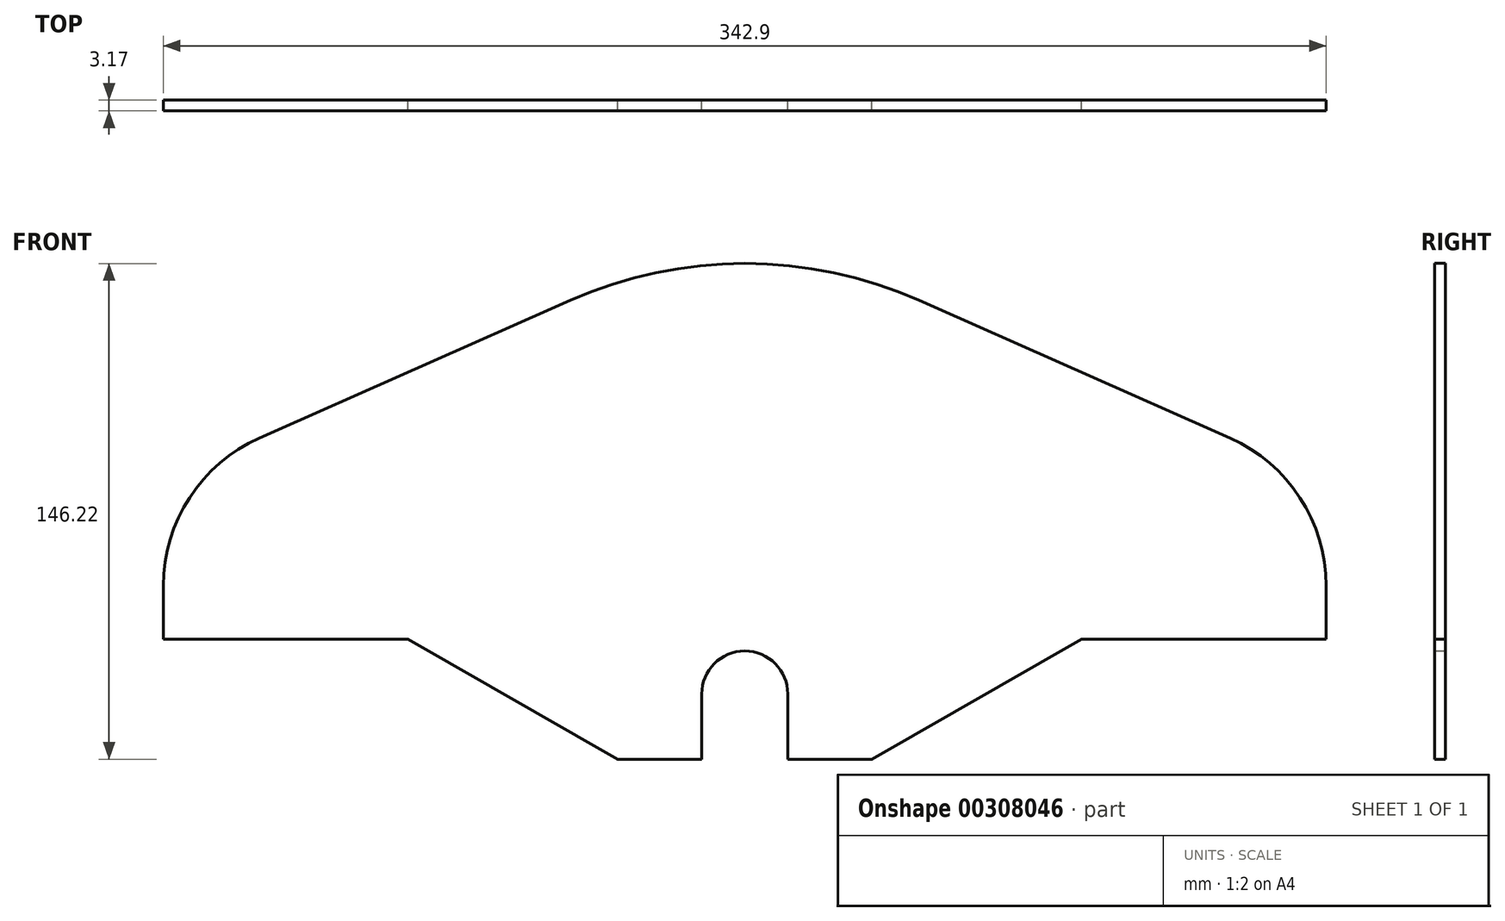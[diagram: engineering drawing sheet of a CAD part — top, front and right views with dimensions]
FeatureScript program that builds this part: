
annotation { "Feature Type Name" : "Feature", "Feature Type Description" : "" }
export const myFeature = defineFeature(function(context is Context, id is Id, definition is map)
    precondition{}
    {
        {
            var Q0;
            Q0=qCreatedBy(makeId("Front.planeOp"),FACE);
            var sketch = newSketch(context, id + "F0", { "sketchPlane" : qUnion([Q0])});
            skLineSegment(sketch, "E0.right", {"start": v(-171.45, -37.68) * mm, "end": v(-171.45, -21.96) * mm, "construction": true});
            skLineSegment(sketch, "E1.0", {"start": v(171.45, -37.68) * mm, "end": v(99.31, -37.68) * mm, "construction": true});
            skArc(sketch, "E2", {"start": v(171.45, -21.96) * mm, "mid": v(163.75, 4.01) * mm, "end": v(143.13, 21.58) * mm});
            skLineSegment(sketch, "E3", {"start": v(143.13, 21.58) * mm, "end": v(51.47, 62.22) * mm});
            skArc(sketch, "E4.trimOffspring", {"start": v(51.47, 62.22) * mm, "mid": v(26.3, 70.36) * mm, "end": v(0, 73.11) * mm});
            skLineSegment(sketch, "E5", {"start": v(99.31, -37.68) * mm, "end": v(171.45, -37.68) * mm});
            skLineSegment(sketch, "E6", {"start": v(37.5, -73.11) * mm, "end": v(99.31, -37.68) * mm});
            skPoint(sketch, "E7.orphan", {"position": v(171.45, 73.11) * mm});
            skLineSegment(sketch, "E8", {"start": v(171.45, -37.68) * mm, "end": v(171.45, -21.96) * mm});
            skLineSegment(sketch, "E9.trimOffspring", {"start": v(-12.7, -73.11) * mm, "end": v(-37.5, -73.11) * mm, "construction": true});
            skLineSegment(sketch, "E10", {"start": v(12.7, -73.11) * mm, "end": v(37.5, -73.11) * mm});
            skArc(sketch, "E11.MirrorCS", {"start": v(-51.47, 62.22) * mm, "mid": v(-26.3, 70.36) * mm, "end": v(0, 73.11) * mm});
            skLineSegment(sketch, "E12.MirrorCS", {"start": v(-143.13, 21.58) * mm, "end": v(-51.47, 62.22) * mm});
            skArc(sketch, "E13.MirrorCS", {"start": v(-171.45, -21.96) * mm, "mid": v(-163.75, 4.01) * mm, "end": v(-143.13, 21.58) * mm});
            skLineSegment(sketch, "E14.MirrorCS", {"start": v(-171.45, -37.68) * mm, "end": v(-171.45, -21.96) * mm});
            skLineSegment(sketch, "E15.MirrorCS", {"start": v(-99.31, -37.68) * mm, "end": v(-171.45, -37.68) * mm});
            skLineSegment(sketch, "E16.MirrorCS", {"start": v(-12.7, -73.11) * mm, "end": v(-37.5, -73.11) * mm});
            skLineSegment(sketch, "E17.MirrorCS", {"start": v(-37.5, -73.11) * mm, "end": v(-99.31, -37.68) * mm});
            skPoint(sketch, "E18.orphan", {"position": v(-171.45, -73.11) * mm});
            skArc(sketch, "E19", {"start": v(12.7, -53.89) * mm, "mid": v(0, -41.19) * mm, "end": v(-12.7, -53.89) * mm});
            skLineSegment(sketch, "E20", {"start": v(-12.7, -53.89) * mm, "end": v(-12.7, -73.11) * mm});
            skLineSegment(sketch, "E21", {"start": v(12.7, -53.89) * mm, "end": v(12.7, -73.11) * mm});
            skSolve(sketch);
        }
        {
            var Q0;
            Q0=makeQuery(id+"F0.imprint","IMPRINT",FACE,{"disambiguationData":[TD([[makeQuery(id+"F0.imprint","IMPRINT",EDGE,{"derivedFrom":sQuery(id+"F0.wireOp",EDGE,"E2")}),1.0]])]});
            extrude(context, id + "F1", {"entities" : qUnion([Q0]), "depth" : 3.17 * mm});
        }
    });
